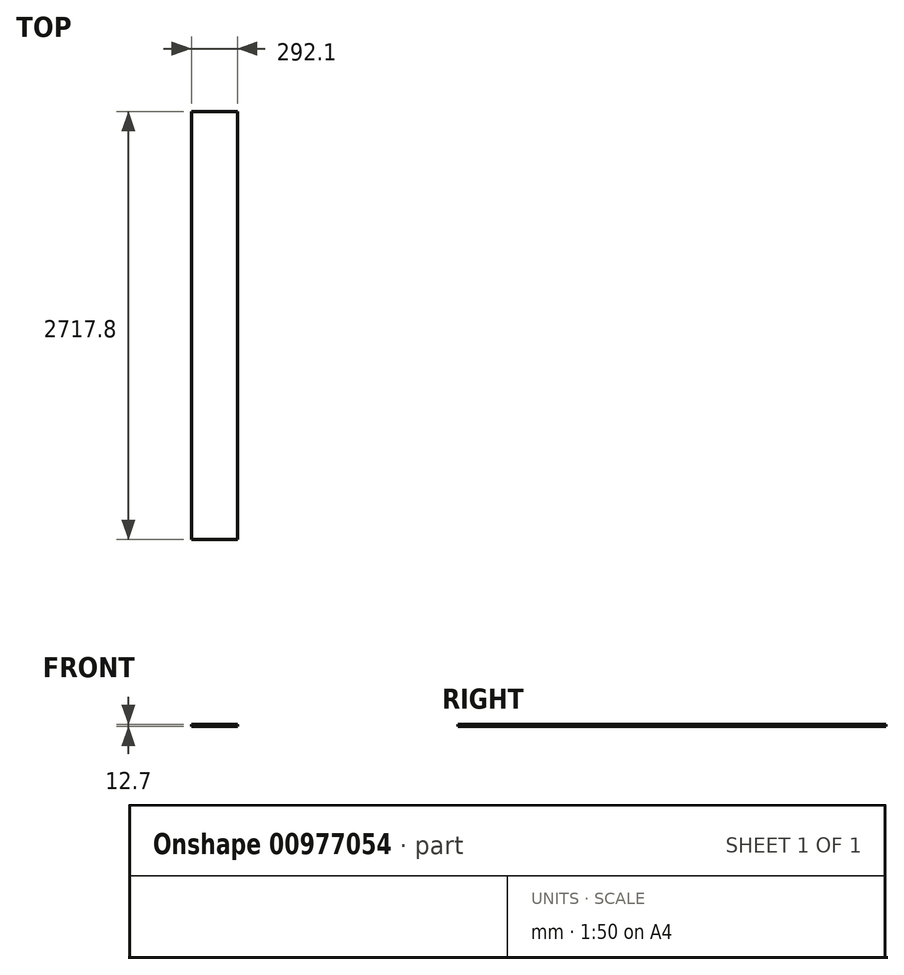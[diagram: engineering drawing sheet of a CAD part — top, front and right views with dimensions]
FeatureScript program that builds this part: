
annotation { "Feature Type Name" : "Feature", "Feature Type Description" : "" }
export const myFeature = defineFeature(function(context is Context, id is Id, definition is map)
    precondition{}
    {
        {
            var Q0;
            Q0=qCreatedBy(makeId("Front.planeOp"),FACE);
            var sketch = newSketch(context, id + "F0", { "sketchPlane" : qUnion([Q0])});
            skLineSegment(sketch, "E0.bottom", {"start": v(146.05, -6.35) * mm, "end": v(-146.05, -6.35) * mm});
            skLineSegment(sketch, "E0.top", {"start": v(146.05, 6.35) * mm, "end": v(-146.05, 6.35) * mm});
            skLineSegment(sketch, "E0.left", {"start": v(146.05, -6.35) * mm, "end": v(146.05, 6.35) * mm});
            skLineSegment(sketch, "E0.right", {"start": v(-146.05, -6.35) * mm, "end": v(-146.05, 6.35) * mm});
            skPoint(sketch, "E0.middle", {"position": v(0, 0) * mm});
            skSolve(sketch);
        }
        {
            var Q0;
            Q0 = qSketchRegion(id + "F0", true);
            extrude(context, id + "F1", {"entities" : qUnion([Q0]), "endBound" : BoundingType.SYMMETRIC, "depth" : 2717.8 * mm, "offsetDistance" : 25.4 * mm});
        }
    });
